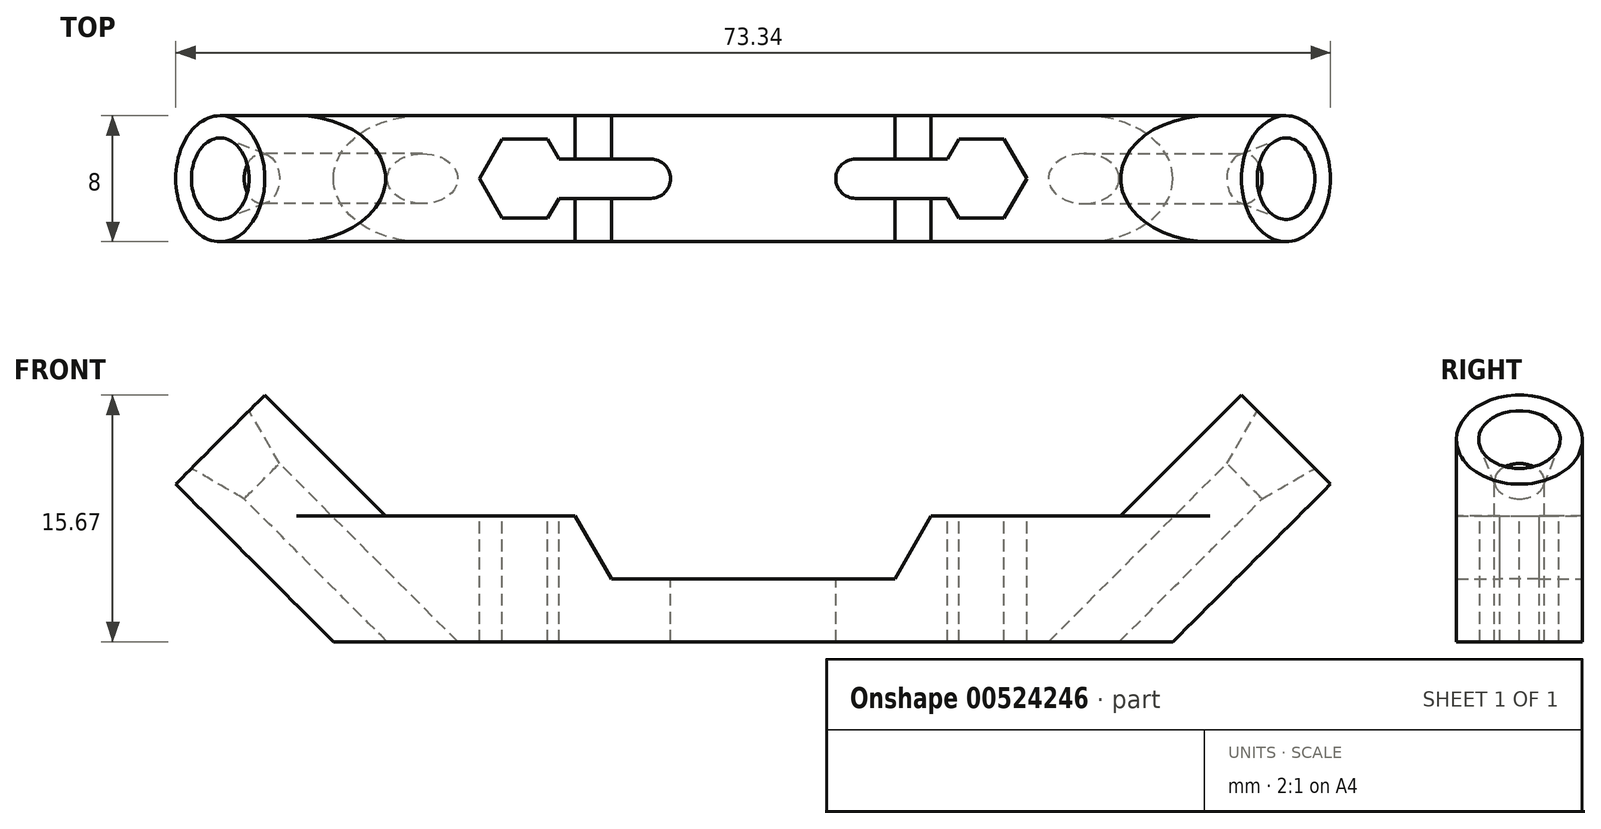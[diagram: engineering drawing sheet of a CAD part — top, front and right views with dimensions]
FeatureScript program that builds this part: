
annotation { "Feature Type Name" : "Feature", "Feature Type Description" : "" }
export const myFeature = defineFeature(function(context is Context, id is Id, definition is map)
    precondition{}
    {
        {
            var Q0;
            Q0=qCreatedBy(makeId("Front.planeOp"),FACE);
            var sketch = newSketch(context, id + "F0", { "sketchPlane" : qUnion([Q0])});
            skLineSegment(sketch, "E0", {"start": v(0, 0) * mm, "end": v(-26.66, 0) * mm});
            skLineSegment(sketch, "E1", {"start": v(-26.66, 0) * mm, "end": v(-34.66, 8) * mm});
            skLineSegment(sketch, "E2", {"start": v(-34.66, 8) * mm, "end": v(0, 8) * mm});
            skLineSegment(sketch, "E3", {"start": v(0, 8) * mm, "end": v(0, 0) * mm});
            skLineSegment(sketch, "E4", {"start": v(-29, 8) * mm, "end": v(-21, 0) * mm, "construction": true});
            skLineSegment(sketch, "E5", {"start": v(0, 8) * mm, "end": v(0, 31.76) * mm, "construction": true});
            skSolve(sketch);
        }
        {
            var Q0;
            Q0=qSketchRegion(id+"F0",true);
            extrude(context, id + "F1", {"entities" : qUnion([Q0]), "endBound" : BoundingType.SYMMETRIC, "depth" : 8 * mm});
        }
        {
            var Q0;
            Q0=makeQuery(id+"F1.opExtrude","CAP_EDGE",EDGE,{"disambiguationData":[OSD([sQuery(id+"F0.wireOp",EDGE,"E1")])],"isStart":true});
            var Q1;
            Q1=makeQuery(id+"F1.opExtrude","CAP_EDGE",EDGE,{"disambiguationData":[OSD([sQuery(id+"F0.wireOp",EDGE,"E1")])],"isStart":false});
            fillet(context, id + "F2", {"entities" : qUnion([Q0, Q1]), "radius" : 4 * mm, "tangentPropagation" : true, "allowEdgeOverflow" : false});
        }
        {
            var Q0;
            Q0=makeQuery(id+"F1.opExtrude","SWEPT_FACE",FACE,{"disambiguationData":[OSD([sQuery(id+"F0.wireOp",EDGE,"E2")])]});
            var sketch = newSketch(context, id + "F3", { "sketchPlane" : qUnion([Q0])});
            skLineSegment(sketch, "E6", {"start": v(-14.5, 0) * mm, "end": v(0, 0) * mm, "construction": true});
            skLineSegment(sketch, "E7", {"start": v(0, 0) * mm, "end": v(0, 20.84) * mm, "construction": true});
            skCircle(sketch, "E8.cCircle", {"center": v(-14.5, 0) * mm, "radius": 2.5 * mm, "construction": true});
            skLineSegment(sketch, "E8.0", {"start": v(-13.06, 2.5) * mm, "end": v(-11.61, 0) * mm});
            skLineSegment(sketch, "E8.1", {"start": v(-11.61, 0) * mm, "end": v(-13.06, -2.5) * mm});
            skLineSegment(sketch, "E8.2", {"start": v(-13.06, -2.5) * mm, "end": v(-15.94, -2.5) * mm});
            skLineSegment(sketch, "E8.3", {"start": v(-15.94, -2.5) * mm, "end": v(-17.39, 0) * mm});
            skLineSegment(sketch, "E8.4", {"start": v(-17.39, 0) * mm, "end": v(-15.94, 2.5) * mm});
            skLineSegment(sketch, "E8.5", {"start": v(-15.94, 2.5) * mm, "end": v(-13.06, 2.5) * mm});
            skPoint(sketch, "E8.0.midPoint", {"position": v(-12.33, 1.25) * mm});
            skSolve(sketch);
        }
        {
            var Q0;
            Q0=qSketchRegion(id+"F3",true);
            extrude(context, id + "F4", {"entities" : qUnion([Q0]), "operationType" : NewBodyOperationType.REMOVE, "endBound" : BoundingType.UP_TO_NEXT, "oppositeDirection" : true, "depth" : 25.4 * mm});
        }
        {
            var Q0;
            Q0=qCreatedBy(makeId("Front.planeOp"),FACE);
            var sketch = newSketch(context, id + "F5", { "sketchPlane" : qUnion([Q0])});
            skLineSegment(sketch, "E9", {"start": v(0, 11.67) * mm, "end": v(0, 4) * mm});
            skLineSegment(sketch, "E10", {"start": v(0, 4) * mm, "end": v(-9, 4) * mm});
            skLineSegment(sketch, "E11", {"start": v(-9, 4) * mm, "end": v(-13.43, 11.67) * mm});
            skLineSegment(sketch, "E12", {"start": v(-13.43, 11.67) * mm, "end": v(0, 11.67) * mm});
            skLineSegment(sketch, "E13", {"start": v(0, 11.67) * mm, "end": v(0, 17.09) * mm, "construction": true});
            skSolve(sketch);
        }
        {
            var Q0;
            Q0=qSketchRegion(id+"F5",true);
            extrude(context, id + "F6", {"entities" : qUnion([Q0]), "operationType" : NewBodyOperationType.REMOVE, "endBound" : BoundingType.SYMMETRIC, "depth" : 25 * mm});
        }
        {
            var Q0;
            Q0=qCreatedBy(makeId("Front.planeOp"),FACE);
            var sketch = newSketch(context, id + "F7", { "sketchPlane" : qUnion([Q0])});
            skLineSegment(sketch, "E14", {"start": v(-10.3, -10.7) * mm, "end": v(-44.62, 23.62) * mm});
            skLineSegment(sketch, "E15", {"start": v(-44.62, 23.62) * mm, "end": v(-45.74, 22.5) * mm});
            skLineSegment(sketch, "E16", {"start": v(-45.74, 22.5) * mm, "end": v(-11.43, -11.81) * mm});
            skLineSegment(sketch, "E17", {"start": v(-11.43, -11.81) * mm, "end": v(-10.3, -10.7) * mm});
            skLineSegment(sketch, "E18", {"start": v(-38.6, 17.6) * mm, "end": v(-44.62, 23.62) * mm, "construction": true});
            skSolve(sketch);
        }
        {
            var Q0;
            Q0=sQuery(id+"F0.wireOp",EDGE,"E4");
            var Q1;
            Q1=sQuery(id+"F0.wireOp",VERTEX,"E4.start");
            cPlane(context, id + "F8", {"entities" : qUnion([Q0, Q1]), "cplaneType" : CPlaneType.LINE_POINT, "offset" : 25 * mm, "width" : 150 * mm, "height" : 150 * mm});
        }
        {
            var Q0;
            Q0=qCreatedBy(id+"F8.planeOp",FACE);
            var sketch = newSketch(context, id + "F9", { "sketchPlane" : qUnion([Q0])});
            skCircle(sketch, "E19", {"center": v(0, -14.85) * mm, "radius": 4 * mm});
            skSolve(sketch);
        }
        {
            var Q0;
            Q0=qSketchRegion(id+"F9",true);
            extrude(context, id + "F10", {"entities" : qUnion([Q0]), "operationType" : NewBodyOperationType.ADD, "endBound" : BoundingType.SYMMETRIC, "oppositeDirection" : true, "depth" : 13.7 * mm});
        }
        {
            var Q0;
            Q0=qSketchRegion(id+"F7",true);
            var Q1;
            Q1=sQuery(id+"F7.wireOp",EDGE,"E14");
            revolve(context, id + "F11", {"operationType" : NewBodyOperationType.REMOVE, "entities" : qUnion([Q0]), "axis" : qUnion([Q1]), "revolveType" : RevolveType.FULL, "oppositeDirection" : true});
        }
        {
            var Q0;
            Q0=makeQuery(id+"F11.boolean.opBoolean","INTERSECT",EDGE,{"derivedFrom":[makeQuery(id+"F10.opExtrude","CAP_FACE",FACE,{"disambiguationData":[OSD([sQuery(id+"F9.wireOp",EDGE,"E19")])],"isStart":false}),makeQuery(id+"F11.opRevolve","SWEPT_FACE",FACE,{"disambiguationData":[OSD([sQuery(id+"F7.wireOp",EDGE,"E16")])]})]});
            chamfer(context, id + "F12", {"entities" : qUnion([Q0]), "chamferType" : ChamferType.OFFSET_ANGLE, "width" : 1 * mm, "oppositeDirection" : false, "angle" : 75 * degree, "tangentPropagation" : true});
        }
        {
            var Q0;
            Q0=makeQuery(id+"F1.opExtrude","SWEPT_FACE",FACE,{"disambiguationData":[OSD([sQuery(id+"F0.wireOp",EDGE,"E2")])]});
            var sketch = newSketch(context, id + "F13", { "sketchPlane" : qUnion([Q0])});
            skLineSegment(sketch, "E20", {"start": v(-14.5, 0) * mm, "end": v(-6.5, 0) * mm});
            skArc(sketch, "E21.0.startCap", {"start": v(-14.5, -1.25) * mm, "mid": v(-15.75, 0) * mm, "end": v(-14.5, 1.25) * mm});
            skArc(sketch, "E21.0.endCap", {"start": v(-6.5, 1.25) * mm, "mid": v(-5.25, 0) * mm, "end": v(-6.5, -1.25) * mm});
            skLineSegment(sketch, "E21.0.left", {"start": v(-14.5, 1.25) * mm, "end": v(-6.5, 1.25) * mm});
            skLineSegment(sketch, "E21.0.right", {"start": v(-14.5, -1.25) * mm, "end": v(-6.5, -1.25) * mm});
            skPoint(sketch, "E22", {"position": v(-14.5, 2.5) * mm});
            skSolve(sketch);
        }
        {
            var Q0;
            Q0=qSketchRegion(id+"F13",true);
            extrude(context, id + "F14", {"entities" : qUnion([Q0]), "operationType" : NewBodyOperationType.REMOVE, "endBound" : BoundingType.THROUGH_ALL, "oppositeDirection" : true, "depth" : 25 * mm});
        }
        {
            var Q0;
            Q0=makeQuery(id+"F1.opExtrude","SWEPT_BODY",BODY,{"disambiguationData":[OSD([sQuery(id+"F0.wireOp",EDGE,"E0"),sQuery(id+"F0.wireOp",EDGE,"E1"),sQuery(id+"F0.wireOp",EDGE,"E2"),sQuery(id+"F0.wireOp",EDGE,"E3")])]});
            var Q1;
            Q1=makeQuery(id+"F1.opExtrude","SWEPT_FACE",FACE,{"disambiguationData":[OSD([sQuery(id+"F0.wireOp",EDGE,"E3")])]});
            mirror(context, id + "F15", {"operationType" : NewBodyOperationType.ADD, "entities" : qUnion([Q0]), "mirrorPlane" : qUnion([Q1])});
        }
    });
